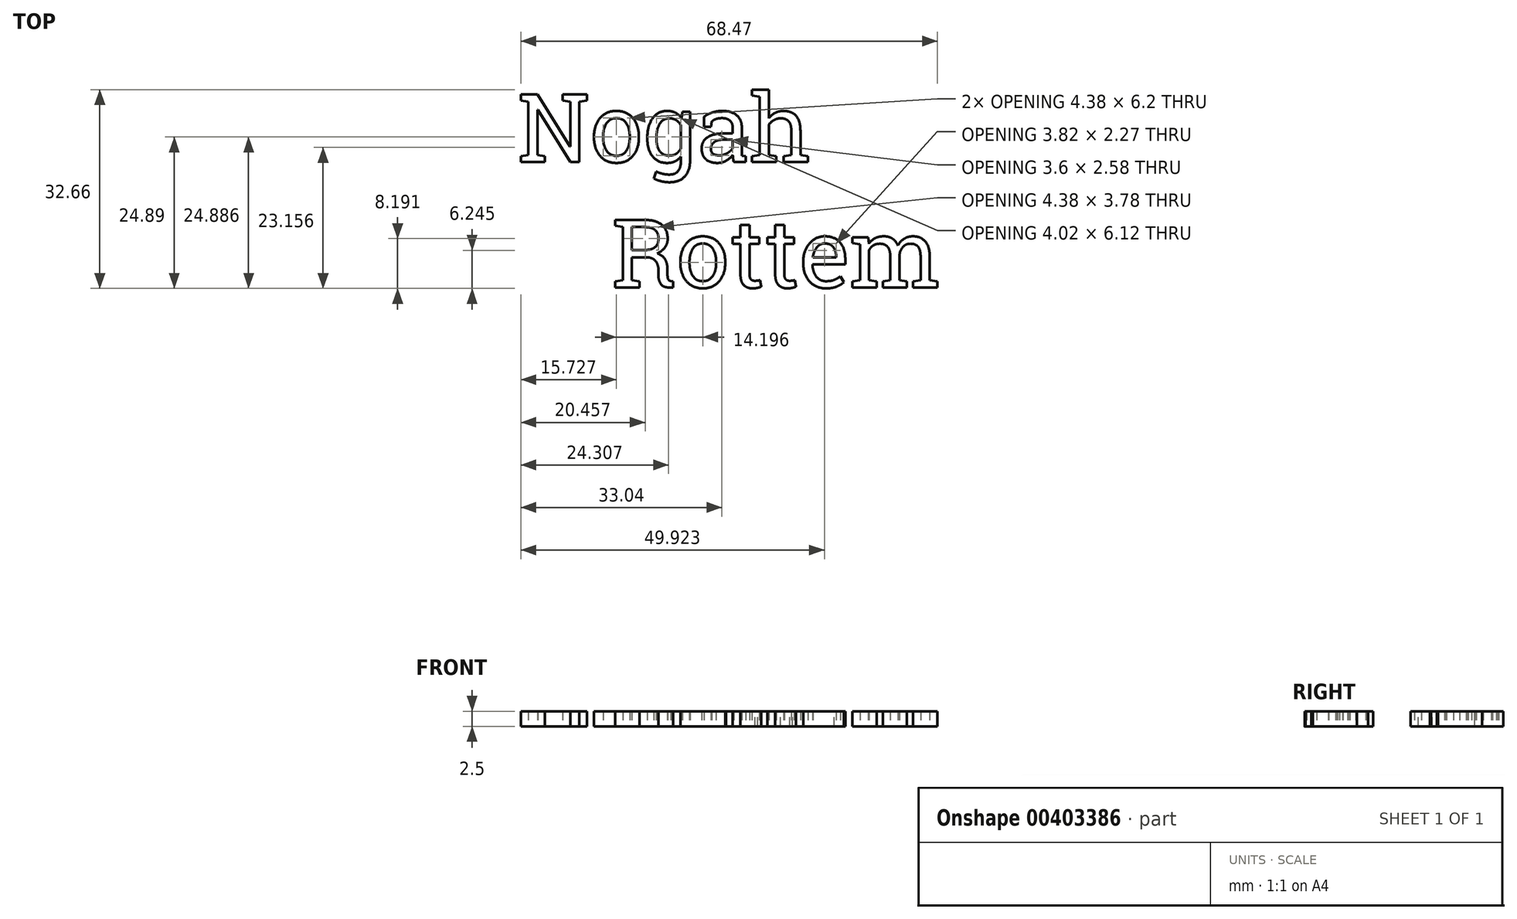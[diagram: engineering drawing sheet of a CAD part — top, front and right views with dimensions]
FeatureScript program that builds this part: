
annotation { "Feature Type Name" : "Feature", "Feature Type Description" : "" }
export const myFeature = defineFeature(function(context is Context, id is Id, definition is map)
    precondition{}
    {
        {
            var Q0;
            Q0=qCreatedBy(makeId("Top.planeOp"),FACE);
            var sketch = newSketch(context, id + "F0", { "sketchPlane" : qUnion([Q0])});
            skText(sketch, "E0", { "text": "Nogah\n    Rottem", "fontName": "RobotoSlab-Regular.ttf"});
            const initialGuessF0  = {"E0": [-0.035, -0.01124, 1, 0, 0.01124]};
            skSetInitialGuess(sketch, initialGuessF0);
            skSolve(sketch);
        }
        {
            var Q0;
            Q0 = qSketchRegion(id + "F0", true);
            extrude(context, id + "F1", {"entities" : qUnion([Q0]), "depth" : 2.5 * mm});
        }
    });
